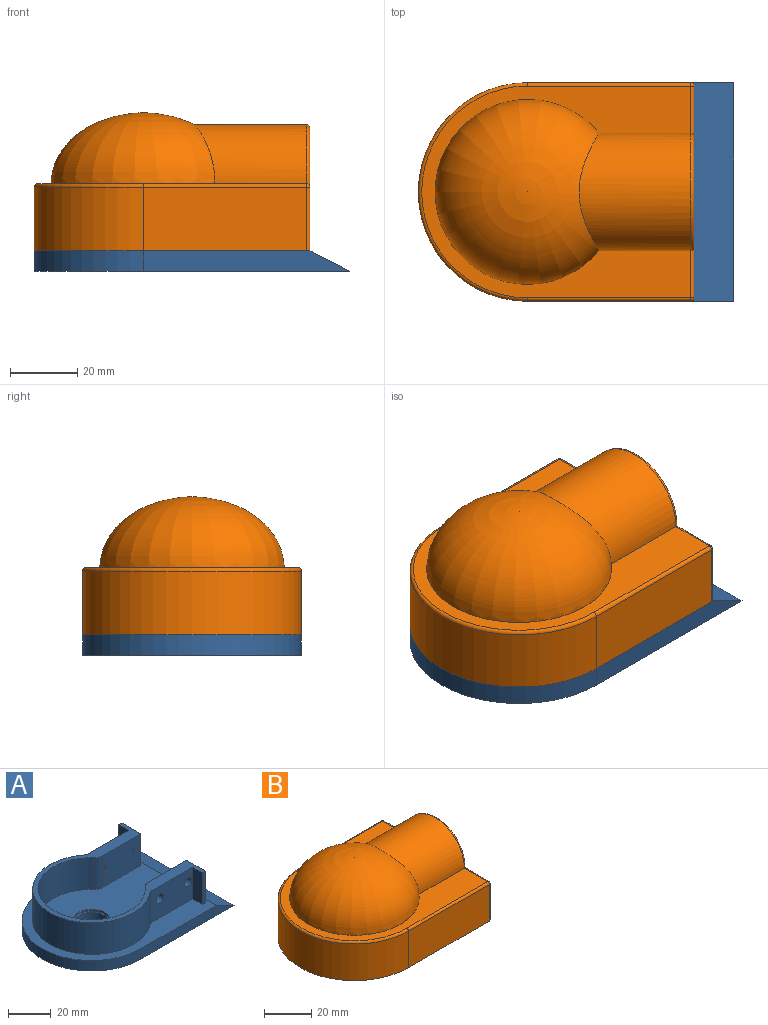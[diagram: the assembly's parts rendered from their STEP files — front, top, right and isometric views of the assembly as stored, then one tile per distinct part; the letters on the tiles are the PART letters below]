
ASSEMBLY  parts=2 mates=1
PART A: 36 faces, bbox 93.8x65x24 mm
  f0: plane 27.74x18mm, normal (0,1,0), area 460.1mm2, adj f4,f5,f12,f17,f30,f32
  f1: plane 27.74x18mm, normal (0,-1,0), area 460.1mm2, adj f5,f6,f12,f17,f24,f26
  f2: plane 18x12.5mm, normal (1,0,0), area 225mm2, adj f3,f11,f12,f17
  f3: plane 18x2mm, normal (0,1,0), area 36mm2, adj f2,f4,f12,f17
  f4: plane 18x6.5mm, normal (-1,0,0), area 117mm2, adj f0,f3,f12,f17
  f5: cylinder r=27.5mm len=55mm, axis (0,0,-1), area 2249.9mm2, adj f0,f1,f12,f17
  f6: plane 18x6.5mm, normal (-1,0,0), area 117mm2, adj f1,f7,f12,f17
  f7: plane 18x2mm, normal (0,-1,0), area 36mm2, adj f6,f8,f12,f17
  f8: plane 18x12.5mm, normal (1,0,0), area 225mm2, adj f7,f9,f12,f17
  f9: plane 25.14x18mm, normal (0,1,0), area 449mm2, adj f8,f12,f17,f20,f22,f23
  f10: cylinder r=25mm len=50mm, axis (0,0,-1), area 2170.7mm2, adj f12,f17,f20,f21
  f11: plane 25.14x18mm, normal (0,-1,0), area 449mm2, adj f2,f12,f17,f21,f28,f29
  f12: plane 75x55mm, normal (0,0,1), area 679.1mm2, adj f0,f1,f2,f3,f4,f5,f6,f7
  f13: plane 61.3x6mm, normal (0,-1,0), area 332.4mm2, adj f16,f17,f18,f19
  f14: plane 61.3x6mm, normal (0,1,0), area 332.4mm2, adj f16,f17,f18,f19
  f15: cylinder r=8.75mm len=17.5mm, axis (0,0,-1), area 55mm2, adj f17,f35
  f16: cylinder r=32.5mm len=65mm, axis (0,0,-1), area 612.6mm2, adj f13,f14,f17,f18
  f17: plane 82x65mm, normal (0,0,1), area 3957.1mm2, adj f0,f1,f2,f3,f4,f5,f6,f7
  f18: plane 93.8x65mm, normal (0,0,-1), area 5442.5mm2, adj f13,f14,f16,f19,f34
  f19: plane 65x11.8mm, normal (0.45,0,0.89), area 860.4mm2, adj f13,f14,f17,f18
  f20: cylinder r=5mm len=18mm, axis (0,0,-1), area 75.7mm2, adj f9,f10,f12,f17
  f21: cylinder r=5mm len=18mm, axis (0,0,-1), area 75.7mm2, adj f10,f11,f12,f17
  f22: cylinder r=0.75mm len=2mm, axis (0,-1,0), area 9.4mm2, adj f9,f27
  f23: cylinder r=0.75mm len=2mm, axis (0,-1,0), area 9.4mm2, adj f9,f25
  f24: cylinder r=2.5mm len=5mm, axis (0,-1,0), area 62.8mm2, adj f1,f25
  f25: plane 5x5mm, normal (0,-1,0), area 17.9mm2, adj f23,f24
  f26: cylinder r=2.5mm len=5mm, axis (0,-1,0), area 62.8mm2, adj f1,f27
  f27: plane 5x5mm, normal (0,-1,0), area 17.9mm2, adj f22,f26
  f28: cylinder r=0.75mm len=2mm, axis (0,1,0), area 9.4mm2, adj f11,f33
  f29: cylinder r=0.75mm len=2mm, axis (0,1,0), area 9.4mm2, adj f11,f31
  f30: cylinder r=2.5mm len=5mm, axis (0,1,0), area 62.8mm2, adj f0,f31
  f31: plane 5x5mm, normal (0,1,0), area 17.9mm2, adj f29,f30
  f32: cylinder r=2.5mm len=5mm, axis (0,1,0), area 62.8mm2, adj f0,f33
  f33: plane 5x5mm, normal (0,1,0), area 17.9mm2, adj f28,f32
  f34: cylinder r=8mm len=16mm, axis (0,0,-1), area 251.3mm2, adj f18,f35
  f35: plane 17.5x17.5mm, normal (0,0,1), area 39.5mm2, adj f15,f34
PART B: 43 faces, bbox 194.7x180.4x148.9 mm
  f0: plane 190x173mm, normal (0,0,1), area 1433.7mm2, adj f1,f2,f38,f39,f40,f41,f42
  f1: revolved ~48.71x45mm, area 606.7mm2, adj f0,f42
  f2: cylinder r=1mm len=15.03mm, axis (0,-1,0), area 22.8mm2, adj f0,f3,f36,f37
  f3: plane 63x36.5mm, normal (1,0,0), area 615.5mm2, adj f2,f4,f27,f31,f33,f34,f35,f37
  f4: cylinder r=1mm len=20mm, axis (0,0,-1), area 31.4mm2, adj f3,f5,f33,f35
  f5: plane 26.14x20mm, normal (0,1,0), area 70.3mm2, adj f4,f6,f24,f25,f26,f33
  f6: cylinder r=5mm len=3.73mm, axis (0,0,-1), area 8.4mm2, adj f5,f7,f23,f24
  f7: bspline ~33.34x16.82mm, area 161.9mm2, adj f6,f8,f22,f26
  f8: cylinder r=5mm len=3.73mm, axis (0,0,-1), area 8.4mm2, adj f7,f9,f23,f24
  f9: plane 26.14x20mm, normal (0,-1,0), area 70.3mm2, adj f8,f10,f24,f26,f33,f34
  f10: plane 18x12.5mm, normal (-1,0,0), area 225mm2, adj f9,f11,f24,f33
  f11: plane 18x2mm, normal (0,-1,0), area 36mm2, adj f10,f12,f24,f33
  f12: plane 18x3mm, normal (-1,0,0), area 54mm2, adj f11,f13,f24,f33
  f13: plane 45.5x18mm, normal (0,-1,0), area 819mm2, adj f12,f14,f24,f33
  f14: cylinder r=30.5mm len=29.43mm, axis (0,0,1), area 716.7mm2, adj f13,f15,f24,f33
  f15: plane 18x3.12mm, normal (0,1,0), area 56.2mm2, adj f14,f16,f24,f33
  f16: cylinder r=27.5mm len=18mm, axis (0,0,1), area 292.2mm2, adj f15,f17,f24,f33
  f17: plane 18x3.12mm, normal (0,-1,0), area 56.2mm2, adj f16,f18,f24,f33
  f18: cylinder r=30.5mm len=29.43mm, axis (0,0,1), area 716.7mm2, adj f17,f19,f24,f33
  f19: plane 45.5x18mm, normal (0,1,0), area 819mm2, adj f18,f20,f24,f33
  f20: plane 18x3mm, normal (-1,0,0), area 54mm2, adj f19,f21,f24,f33
  f21: plane 18x2mm, normal (0,1,0), area 36mm2, adj f20,f24,f25,f33
  f22: revolved ~43.61x41.64mm, area 526.9mm2, adj f7,f23
  f23: cylinder r=25mm len=50mm, axis (0,0,-1), area 241.2mm2, adj f6,f8,f22,f24
  f24: plane 76.93x61mm, normal (0,0,-1), area 1610.3mm2, adj f5,f6,f8,f9,f10,f11,f12,f13
  f25: plane 18x12.5mm, normal (-1,0,0), area 225mm2, adj f5,f21,f24,f33
  f26: cylinder r=15mm len=32.55mm, axis (1,0,0), area 1375.5mm2, adj f5,f7,f9,f35
  f27: cylinder r=1mm len=19mm, axis (0,0,-1), area 29.8mm2, adj f3,f28,f33,f36
  f28: plane 48.5x19mm, normal (0,-1,0), area 921.5mm2, adj f27,f29,f33,f38
  f29: cylinder r=32.5mm len=65mm, axis (0,0,-1), area 1939.9mm2, adj f28,f30,f33,f39
  f30: plane 48.5x19mm, normal (0,1,0), area 921.5mm2, adj f29,f31,f33,f40
  f31: cylinder r=1mm len=19mm, axis (0,0,1), area 29.8mm2, adj f3,f30,f32,f33
  f32: sphere r=1mm, area 1.6mm2, adj f31,f40,f41
  f33: plane 82x65mm, normal (0,0,-1), area 517.7mm2, adj f3,f4,f5,f9,f10,f11,f12,f13
  f34: cylinder r=1mm len=20mm, axis (0,0,1), area 31.4mm2, adj f3,f9,f33,f35
  f35: torus R=16mm, axis (1,0,0), area 75.8mm2, adj f3,f4,f26,f34
  f36: sphere r=1mm, area 1.6mm2, adj f2,f27,f38
  f37: torus R=16.5mm, axis (1,0,0), area 86.2mm2, adj f2,f3,f41,f42
  f38: cylinder r=1mm len=48.5mm, axis (-1,0,0), area 76.2mm2, adj f0,f28,f36,f39
  f39: torus R=31.5mm, axis (0,0,1), area 158.6mm2, adj f0,f29,f38,f40
  f40: cylinder r=1mm len=48.5mm, axis (1,0,0), area 76.2mm2, adj f0,f30,f32,f39
  f41: cylinder r=1mm len=15.03mm, axis (0,1,0), area 22.8mm2, adj f0,f3,f32,f37
  f42: cylinder r=17.5mm len=35mm, axis (1,0,0), area 1655.7mm2, adj f0,f1,f37
PLACE A t=(-17.12,-3.1,-13.29)mm fixed
PLACE B t=(-17.12,-3.1,10.71)mm
MATE fastened A.f5 <-> B.f14  axis (0,0,-1) through (-17.12,-3.1,10.71)mm
